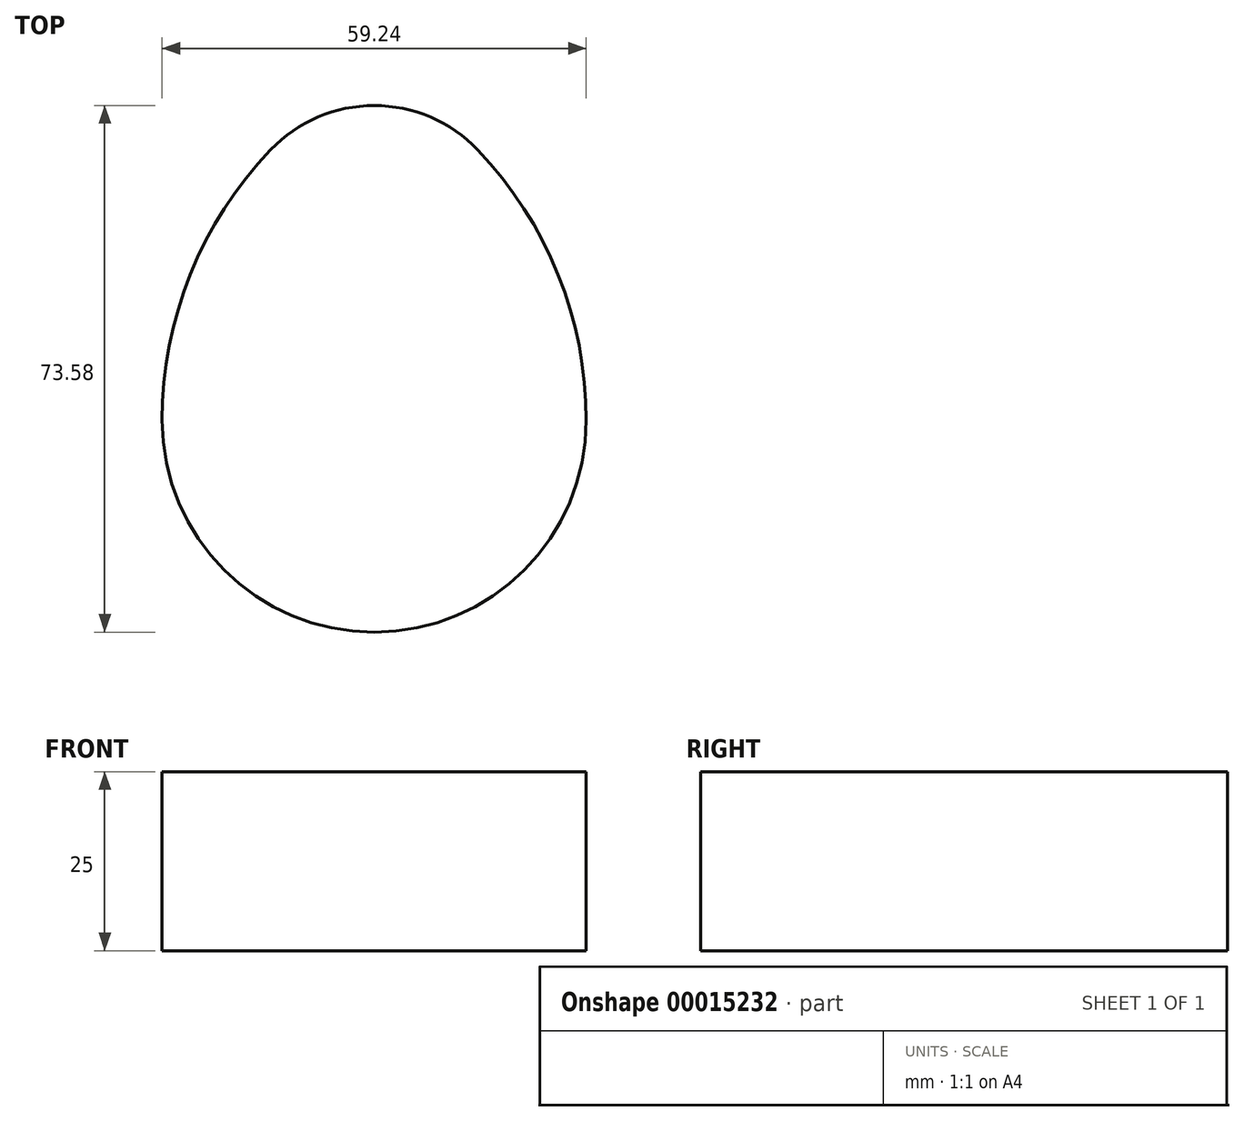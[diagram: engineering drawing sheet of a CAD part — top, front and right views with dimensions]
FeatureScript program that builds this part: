
annotation { "Feature Type Name" : "Feature", "Feature Type Description" : "" }
export const myFeature = defineFeature(function(context is Context, id is Id, definition is map)
    precondition{}
    {
        {
            var Q0;
            Q0=qCreatedBy(makeId("Top.planeOp"),FACE);
            var sketch = newSketch(context, id + "F0", { "sketchPlane" : qUnion([Q0])});
            skArc(sketch, "E0", {"start": v(-29.62, 0) * mm, "mid": v(0, -29.62) * mm, "end": v(29.62, 0) * mm});
            skArc(sketch, "E1", {"start": v(-14.45, 37.8) * mm, "mid": v(-25.69, 20.36) * mm, "end": v(-29.62, 0) * mm});
            skArc(sketch, "E2.MirrorCS", {"start": v(14.45, 37.8) * mm, "mid": v(25.69, 20.36) * mm, "end": v(29.62, 0) * mm});
            skPoint(sketch, "E3.visualSharp", {"position": v(0, 48.58) * mm});
            skArc(sketch, "E3.filletArc", {"start": v(14.45, 37.8) * mm, "mid": v(0, 43.96) * mm, "end": v(-14.45, 37.8) * mm});
            skSolve(sketch);
        }
        {
            var Q0;
            Q0=makeQuery(id+"F0.imprint","IMPRINT",FACE,{"disambiguationData":[TD([[makeQuery(id+"F0.imprint","IMPRINT",EDGE,{"derivedFrom":sQuery(id+"F0.wireOp",EDGE,"E0")}),1.0]])]});
            extrude(context, id + "F1", {"entities" : qUnion([Q0]), "depth" : 25 * mm});
        }
    });
